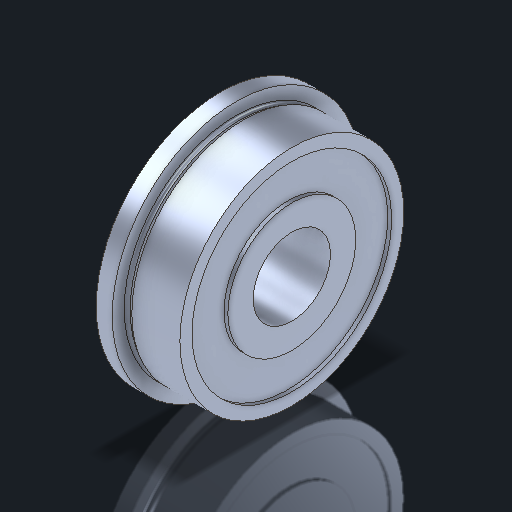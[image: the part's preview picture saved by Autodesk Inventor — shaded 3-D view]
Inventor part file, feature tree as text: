
AUTODESK INVENTOR PART (.ipt)
format: ipt  version: 2023.2 (Build 272271030, 271C)  size: 214,016 bytes
history: native  units: in
note: dims shown in document units (in); Inventor stores cm internally (conversion verified against a paired STEP export)
features: revolve x1
ambient origin geometry x8: Origin, YZ Plane, XZ Plane, XY Plane, X Axis, Y Axis, Z Axis, Center Point
bodies: Solid1 (feature_tree)
feature tree (1):
  revolve  "Revolve1"  [1 undecoded]
note: 1 required parameter value undecoded (feature->parameter linkage not recoverable at this tier; creation-order binding heuristic only, values carry confidence <= 0.55)
